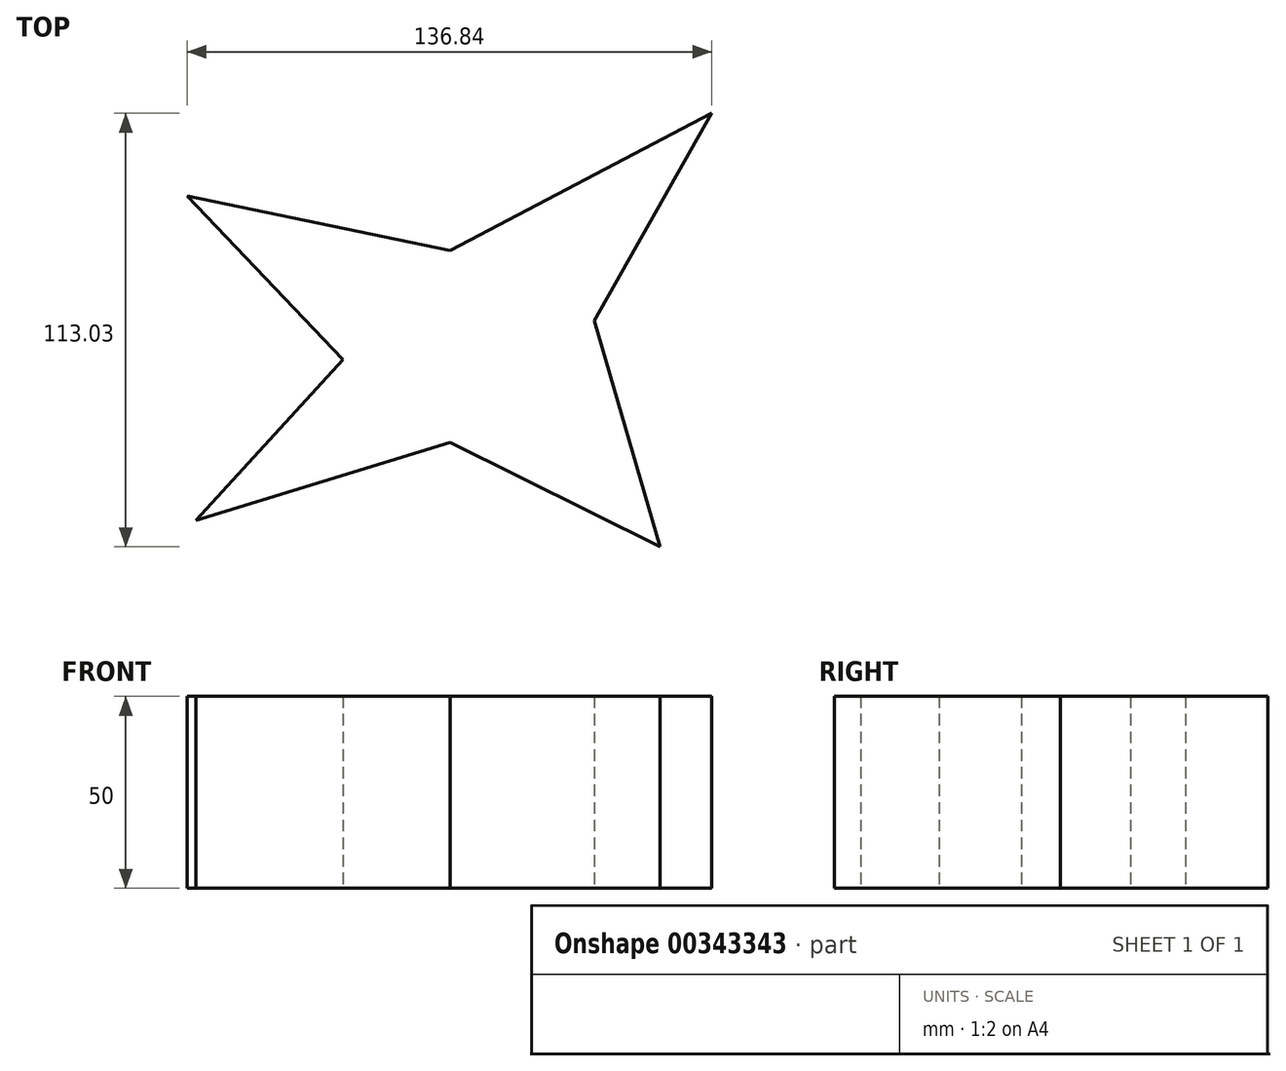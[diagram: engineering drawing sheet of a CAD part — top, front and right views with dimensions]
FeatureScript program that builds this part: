
annotation { "Feature Type Name" : "Feature", "Feature Type Description" : "" }
export const myFeature = defineFeature(function(context is Context, id is Id, definition is map)
    precondition{}
    {
        {
            var Q0;
            Q0=qCreatedBy(makeId("Top.planeOp"),FACE);
            var sketch = newSketch(context, id + "F0", { "sketchPlane" : qUnion([Q0])});
            skLineSegment(sketch, "E0", {"start": v(-68.31, 38.57) * mm, "end": v(-27.58, -4.18) * mm});
            skLineSegment(sketch, "E1", {"start": v(-27.58, -4.18) * mm, "end": v(-66.02, -46.06) * mm});
            skLineSegment(sketch, "E2", {"start": v(-66.02, -46.06) * mm, "end": v(0.25, -25.7) * mm});
            skLineSegment(sketch, "E3", {"start": v(0.25, -25.7) * mm, "end": v(55.05, -52.95) * mm});
            skLineSegment(sketch, "E4", {"start": v(55.05, -52.95) * mm, "end": v(37.83, 6) * mm});
            skLineSegment(sketch, "E5", {"start": v(37.83, 6) * mm, "end": v(68.53, 60.08) * mm});
            skLineSegment(sketch, "E6", {"start": v(68.53, 60.08) * mm, "end": v(0.25, 24.22) * mm});
            skLineSegment(sketch, "E7", {"start": v(0.25, 24.22) * mm, "end": v(-68.31, 38.57) * mm});
            skSolve(sketch);
        }
        {
            var Q0;
            Q0=makeQuery(id+"F0.imprint","IMPRINT",FACE,{"disambiguationData":[TD([[makeQuery(id+"F0.imprint","IMPRINT",EDGE,{"derivedFrom":sQuery(id+"F0.wireOp",EDGE,"E0")}),1.0]])]});
            extrude(context, id + "F1", {"entities" : qUnion([Q0]), "depth" : 50 * mm});
        }
    });
